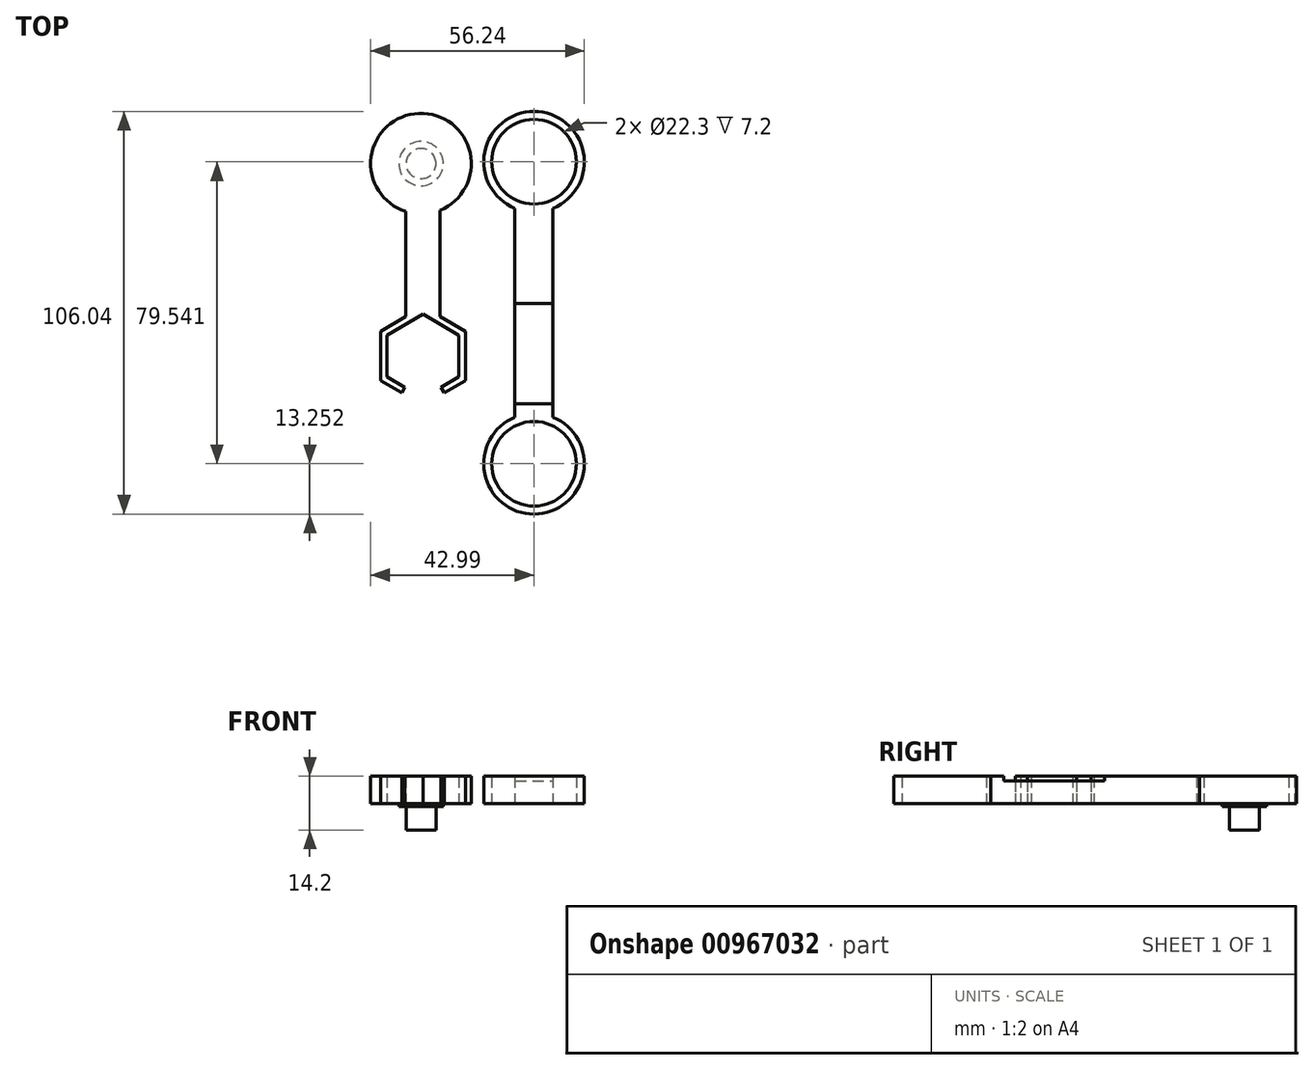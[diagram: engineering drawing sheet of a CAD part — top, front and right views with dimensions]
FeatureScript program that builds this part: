
annotation { "Feature Type Name" : "Feature", "Feature Type Description" : "" }
export const myFeature = defineFeature(function(context is Context, id is Id, definition is map)
    precondition{}
    {
        {
            var Q0;
            Q0=qCreatedBy(makeId("Top.planeOp"),FACE);
            var sketch = newSketch(context, id + "F0", { "sketchPlane" : qUnion([Q0])});
            skLineSegment(sketch, "E0.left", {"start": v(-33.74, 50.67) * mm, "end": v(-33.74, 21.03) * mm});
            skLineSegment(sketch, "E0.right", {"start": v(-24.74, 51.03) * mm, "end": v(-24.74, 21.03) * mm});
            skCircle(sketch, "E1", {"center": v(-29.74, 63.3) * mm, "radius": 13.25 * mm});
            skCircle(sketch, "E2.cCircle", {"center": v(-29.24, 12.66) * mm, "radius": 9.5 * mm, "construction": true});
            skLineSegment(sketch, "E2.0", {"start": v(-19.74, 18.14) * mm, "end": v(-19.74, 7.17) * mm});
            skLineSegment(sketch, "E2.1", {"start": v(-19.74, 7.17) * mm, "end": v(-24.49, 4.43) * mm});
            skLineSegment(sketch, "E2.2", {"start": v(-33.99, 4.43) * mm, "end": v(-38.74, 7.17) * mm});
            skLineSegment(sketch, "E2.3", {"start": v(-38.74, 7.17) * mm, "end": v(-38.74, 18.14) * mm});
            skLineSegment(sketch, "E2.4", {"start": v(-38.74, 18.14) * mm, "end": v(-29.24, 23.63) * mm});
            skLineSegment(sketch, "E2.5", {"start": v(-29.24, 23.63) * mm, "end": v(-19.74, 18.14) * mm});
            skPoint(sketch, "E2.0.midPoint", {"position": v(-19.74, 12.66) * mm});
            skLineSegment(sketch, "E3", {"start": v(-29.24, 23.63) * mm, "end": v(-29.24, 1.69) * mm});
            skCircle(sketch, "E4.cCircle", {"center": v(-29.24, 12.66) * mm, "radius": 11.19 * mm, "construction": true});
            skLineSegment(sketch, "E4.0", {"start": v(-40.43, 19.12) * mm, "end": v(-29.24, 25.58) * mm});
            skLineSegment(sketch, "E4.1", {"start": v(-29.24, 25.58) * mm, "end": v(-18.05, 19.12) * mm});
            skLineSegment(sketch, "E4.2", {"start": v(-18.05, 19.12) * mm, "end": v(-18.05, 6.2) * mm});
            skLineSegment(sketch, "E4.3", {"start": v(-18.05, 6.2) * mm, "end": v(-23.65, 2.97) * mm});
            skLineSegment(sketch, "E4.4", {"start": v(-34.83, 2.97) * mm, "end": v(-40.43, 6.2) * mm});
            skLineSegment(sketch, "E4.5", {"start": v(-40.43, 6.2) * mm, "end": v(-40.43, 19.12) * mm});
            skPoint(sketch, "E4.0.midPoint", {"position": v(-34.83, 22.35) * mm});
            skPoint(sketch, "E5.orphan", {"position": v(-29.24, -0.26) * mm});
            skLineSegment(sketch, "E6", {"start": v(-33.99, 4.43) * mm, "end": v(-34.83, 2.97) * mm});
            skLineSegment(sketch, "E7", {"start": v(-23.65, 2.97) * mm, "end": v(-24.49, 4.43) * mm});
            skCircle(sketch, "E8", {"center": v(-29.74, 63.3) * mm, "radius": 5.85 * mm});
            skCircle(sketch, "E9", {"center": v(-29.74, 63.3) * mm, "radius": 3.95 * mm});
            skLineSegment(sketch, "E10", {"start": v(-29.24, -0.26) * mm, "end": v(-29.24, 76.54) * mm, "construction": true});
            skSolve(sketch);
        }
        {
            var Q0;
            Q0=qCreatedBy(makeId("Top.planeOp"),FACE);
            var sketch = newSketch(context, id + "F1", { "sketchPlane" : qUnion([Q0])});
            skLineSegment(sketch, "E11.left", {"start": v(-5, 51.51) * mm, "end": v(-5, -3.49) * mm});
            skLineSegment(sketch, "E11.right", {"start": v(5, 51.51) * mm, "end": v(5, -3.49) * mm});
            skCircle(sketch, "E12", {"center": v(0, 63.78) * mm, "radius": 11.15 * mm});
            skCircle(sketch, "E13", {"center": v(0, 63.78) * mm, "radius": 13.25 * mm});
            skCircle(sketch, "E14", {"center": v(0, -15.76) * mm, "radius": 11.15 * mm});
            skArc(sketch, "E15", {"start": v(-5, -3.49) * mm, "mid": v(0, -29) * mm, "end": v(5, -3.49) * mm});
            skLineSegment(sketch, "E16", {"start": v(-36.54, 26.44) * mm, "end": v(12.6, 26.44) * mm});
            skLineSegment(sketch, "E17", {"start": v(12.6, 26.44) * mm, "end": v(-36.54, 26.44) * mm});
            skLineSegment(sketch, "E18", {"start": v(-37.79, 0) * mm, "end": v(16.15, 0) * mm});
            skLineSegment(sketch, "E19", {"start": v(16.15, 0) * mm, "end": v(16.15, 26.44) * mm});
            skLineSegment(sketch, "E20", {"start": v(16.15, 26.44) * mm, "end": v(12.6, 26.44) * mm});
            skLineSegment(sketch, "E21", {"start": v(0, 77.03) * mm, "end": v(0, -29) * mm, "construction": true});
            skSolve(sketch);
        }
        {
            var Q0;
            Q0=makeQuery(id+"F1.imprint","IMPRINT",FACE,{"disambiguationData":[TD([[makeQuery(id+"F1.imprint","IMPRINT",EDGE,{"derivedFrom":sQuery(id+"F1.wireOp",EDGE,"E12")}),-1.0]])]});
            var Q1;
            Q1=makeQuery(id+"F1.imprint","IMPRINT",FACE,{"disambiguationData":[TD([[makeQuery(id+"F1.imprint","IMPRINT",EDGE,{"derivedFrom":sQuery(id+"F1.wireOp",EDGE,"E14")}),-1.0]])]});
            var Q2;
            {var subQ0=sQuery(id+"F1.wireOp",EDGE,"E13");var subQ1=sQuery(id+"F1.wireOp",EDGE,"E11.left");var subQ2=makeQuery(id+"F1.imprint","INTERSECT",VERTEX,{"derivedFrom":[subQ1,subQ0]});Q2=makeQuery(id+"F1.imprint","IMPRINT",FACE,{"disambiguationData":[TD([[makeQuery(id+"F1.imprint","IMPRINT",EDGE,{"disambiguationData":[TD([[subQ2,-1.0]])],"derivedFrom":subQ1}),1.0]])]});}
            extrude(context, id + "F2", {"entities" : qUnion([Q0, Q1, Q2]), "flatOperationType" : FlatOperationType.REMOVE, "depth" : 7.2 * mm, "offsetDistance" : 25 * mm, "domain" : OperationDomain.MODEL});
        }
        {
            var Q0;
            {var subQ3=sQuery(id+"F0.wireOp",EDGE,"E0.left");var subQ5=sQuery(id+"F0.wireOp",EDGE,"E1");var subQ6=makeQuery(id+"F0.imprint","INTERSECT",VERTEX,{"derivedFrom":[subQ3,subQ5]});Q0=makeQuery(id+"F0.imprint","IMPRINT",FACE,{"disambiguationData":[TD([[makeQuery(id+"F0.imprint","IMPRINT",EDGE,{"disambiguationData":[TD([[subQ6,-1.0]])],"derivedFrom":subQ3}),1.0]])]});}
            var Q1;
            Q1=makeQuery(id+"F0.imprint","IMPRINT",FACE,{"disambiguationData":[TD([[makeQuery(id+"F0.imprint","IMPRINT",EDGE,{"derivedFrom":sQuery(id+"F0.wireOp",EDGE,"8d993f8e-7f1d-4ff2-8b2e-73f02e62282e")}),-1.0]])]});
            var Q2;
            Q2=makeQuery(id+"F0.imprint","IMPRINT",FACE,{"disambiguationData":[TD([[makeQuery(id+"F0.imprint","IMPRINT",EDGE,{"derivedFrom":sQuery(id+"F0.wireOp",EDGE,"E2.2")}),1.0]])]});
            var Q3;
            {var subQ3=sQuery(id+"F0.wireOp",EDGE,"E2.0");Q3=makeQuery(id+"F0.imprint","IMPRINT",FACE,{"disambiguationData":[TD([[makeQuery(id+"F0.imprint","IMPRINT",EDGE,{"derivedFrom":subQ3}),1.0]])]});}
            var Q4;
            {var subQ0=sQuery(id+"F0.wireOp",EDGE,"E2.4");var subQ1=sQuery(id+"F0.wireOp",EDGE,"E0.left");var subQ2=makeQuery(id+"F0.imprint","INTERSECT",VERTEX,{"derivedFrom":[subQ1,subQ0]});Q4=makeQuery(id+"F0.imprint","IMPRINT",FACE,{"disambiguationData":[TD([[makeQuery(id+"F0.imprint","IMPRINT",EDGE,{"disambiguationData":[TD([[subQ2,1.0]])],"derivedFrom":subQ1}),1.0]])]});}
            var Q5;
            Q5=makeQuery(id+"F0.imprint","IMPRINT",FACE,{"disambiguationData":[TD([[makeQuery(id+"F0.imprint","IMPRINT",EDGE,{"derivedFrom":sQuery(id+"F0.wireOp",EDGE,"E8")}),-1.0]])]});
            var Q6;
            Q6=makeQuery(id+"F0.imprint","IMPRINT",FACE,{"disambiguationData":[TD([[makeQuery(id+"F0.imprint","IMPRINT",EDGE,{"derivedFrom":sQuery(id+"F0.wireOp",EDGE,"E8")}),1.0]])]});
            var Q7;
            Q7=makeQuery(id+"F0.imprint","IMPRINT",FACE,{"disambiguationData":[TD([[makeQuery(id+"F0.imprint","IMPRINT",EDGE,{"derivedFrom":sQuery(id+"F0.wireOp",EDGE,"E9")}),1.0]])]});
            extrude(context, id + "F3", {"entities" : qUnion([Q0, Q1, Q2, Q3, Q4, Q5, Q6, Q7]), "depth" : 7.2 * mm, "offsetDistance" : 25 * mm});
        }
        {
            var Q0;
            Q0=makeQuery(id+"F0.imprint","IMPRINT",FACE,{"disambiguationData":[TD([[makeQuery(id+"F0.imprint","IMPRINT",EDGE,{"derivedFrom":sQuery(id+"F0.wireOp",EDGE,"E8")}),1.0]])]});
            extrude(context, id + "F4", {"entities" : qUnion([Q0]), "operationType" : NewBodyOperationType.ADD, "flatOperationType" : FlatOperationType.REMOVE, "oppositeDirection" : true, "depth" : .8 * mm, "offsetDistance" : 25 * mm, "domain" : OperationDomain.MODEL});
        }
        {
            var Q0;
            Q0=makeQuery(id+"F0.imprint","IMPRINT",FACE,{"disambiguationData":[TD([[makeQuery(id+"F0.imprint","IMPRINT",EDGE,{"derivedFrom":sQuery(id+"F0.wireOp",EDGE,"E9")}),1.0]])]});
            extrude(context, id + "F5", {"entities" : qUnion([Q0]), "operationType" : NewBodyOperationType.ADD, "flatOperationType" : FlatOperationType.REMOVE, "oppositeDirection" : true, "depth" : 7 * mm, "offsetDistance" : 25 * mm, "domain" : OperationDomain.MODEL});
        }
        {
            var Q0;
            {var subQ0=sQuery(id+"F1.wireOp",EDGE,"E17");var subQ1=sQuery(id+"F1.wireOp",EDGE,"E11.left");var subQ2=makeQuery(id+"F1.imprint","INTERSECT",VERTEX,{"derivedFrom":[subQ1,subQ0]});Q0=makeQuery(id+"F1.imprint","IMPRINT",FACE,{"disambiguationData":[TD([[makeQuery(id+"F1.imprint","IMPRINT",EDGE,{"disambiguationData":[TD([[subQ2,-1.0]])],"derivedFrom":subQ1}),1.0]])]});}
            extrude(context, id + "F6", {"entities" : qUnion([Q0]), "operationType" : NewBodyOperationType.ADD, "depth" : 6 * mm, "offsetDistance" : 25 * mm});
        }
    });
